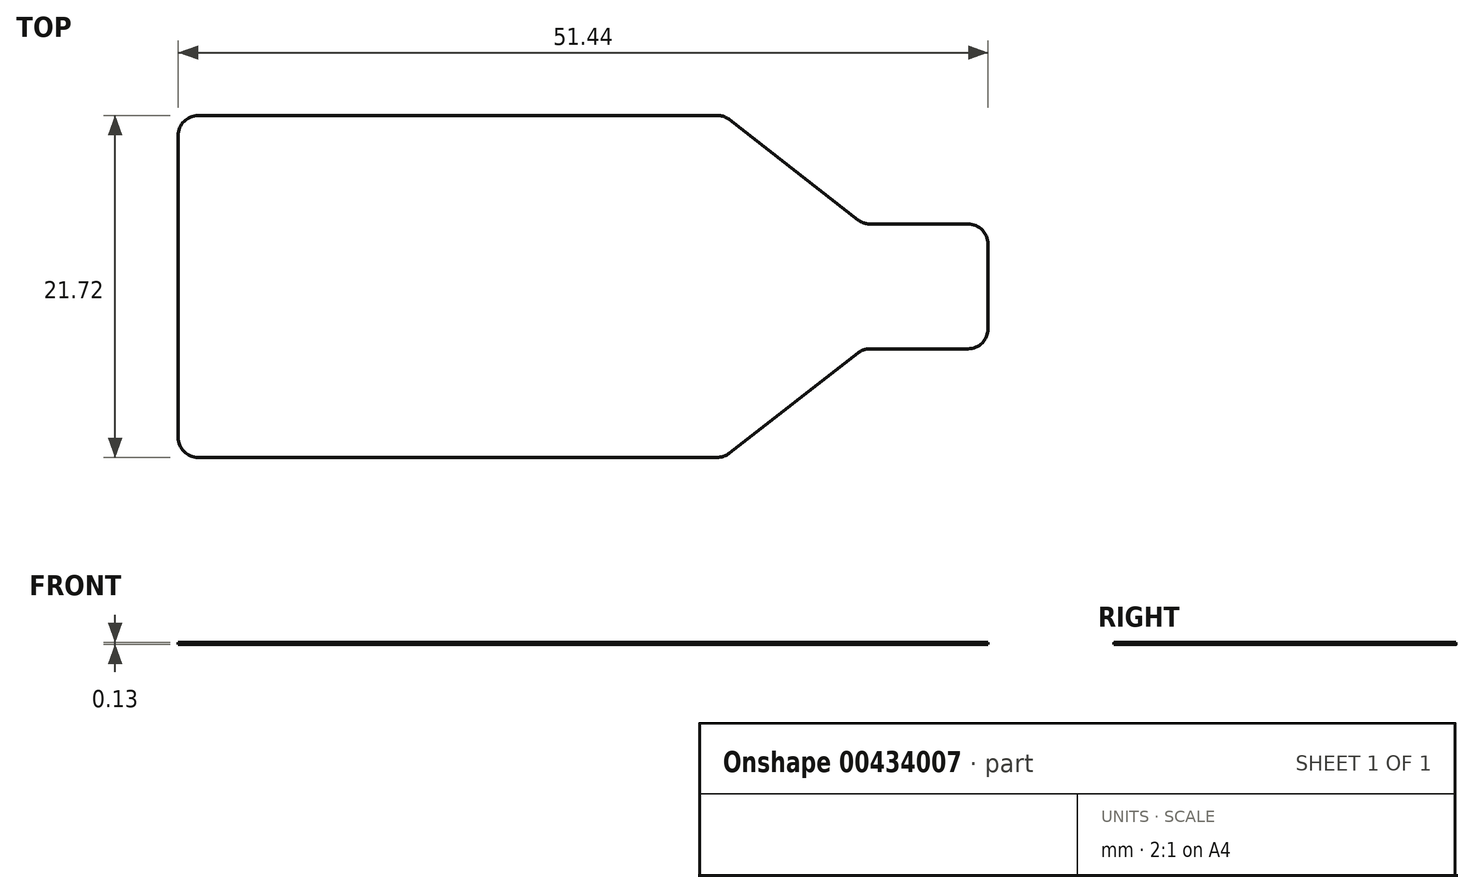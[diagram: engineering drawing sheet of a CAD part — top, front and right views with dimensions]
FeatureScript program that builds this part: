
annotation { "Feature Type Name" : "Feature", "Feature Type Description" : "" }
export const myFeature = defineFeature(function(context is Context, id is Id, definition is map)
    precondition{}
    {
        {
            var Q0;
            Q0=qCreatedBy(makeId("Top.planeOp"),FACE);
            var sketch = newSketch(context, id + "F0", { "sketchPlane" : qUnion([Q0])});
            skLineSegment(sketch, "E0", {"start": v(0, 0) * mm, "end": v(-58.06, 0) * mm, "construction": true});
            skLineSegment(sketch, "E1", {"start": v(0, 0) * mm, "end": v(0, -2.7) * mm});
            skLineSegment(sketch, "E2", {"start": v(-1.27, -3.96) * mm, "end": v(-7.49, -3.96) * mm});
            skLineSegment(sketch, "E3", {"start": v(-8.27, -4.23) * mm, "end": v(-16.42, -10.59) * mm});
            skLineSegment(sketch, "E4", {"start": v(-50.16, -10.86) * mm, "end": v(-17.2, -10.86) * mm});
            skLineSegment(sketch, "E5", {"start": v(-51.44, -9.59) * mm, "end": v(-51.44, 0) * mm});
            skLineSegment(sketch, "E6.MirrorCS", {"start": v(0, 0) * mm, "end": v(0, 2.7) * mm});
            skLineSegment(sketch, "E7.MirrorCS", {"start": v(-1.27, 3.96) * mm, "end": v(-7.49, 3.96) * mm});
            skLineSegment(sketch, "E8.MirrorCS", {"start": v(-8.27, 4.23) * mm, "end": v(-16.42, 10.59) * mm});
            skLineSegment(sketch, "E9.MirrorCS", {"start": v(-17.2, 10.86) * mm, "end": v(-50.17, 10.86) * mm});
            skLineSegment(sketch, "E10.MirrorCS", {"start": v(-51.44, 9.59) * mm, "end": v(-51.44, 0) * mm});
            skPoint(sketch, "E11.visualSharp", {"position": v(-51.44, 10.86) * mm});
            skArc(sketch, "E11.filletArc", {"start": v(-50.17, 10.86) * mm, "mid": v(-51.06, 10.49) * mm, "end": v(-51.44, 9.59) * mm});
            skPoint(sketch, "E12.visualSharp", {"position": v(-51.44, -10.86) * mm});
            skArc(sketch, "E12.filletArc", {"start": v(-51.44, -9.59) * mm, "mid": v(-51.06, -10.49) * mm, "end": v(-50.16, -10.86) * mm});
            skPoint(sketch, "E13.visualSharp", {"position": v(0, 3.96) * mm});
            skArc(sketch, "E13.filletArc", {"start": v(0, 2.7) * mm, "mid": v(-0.37, 3.6) * mm, "end": v(-1.27, 3.96) * mm});
            skPoint(sketch, "E14.visualSharp", {"position": v(0, -3.96) * mm});
            skArc(sketch, "E14.filletArc", {"start": v(-1.27, -3.96) * mm, "mid": v(-0.37, -3.6) * mm, "end": v(0, -2.7) * mm});
            skPoint(sketch, "E15.visualSharp", {"position": v(-7.92, 3.96) * mm});
            skArc(sketch, "E15.filletArc", {"start": v(-8.27, 4.23) * mm, "mid": v(-7.9, 4.03) * mm, "end": v(-7.49, 3.96) * mm});
            skPoint(sketch, "E16.visualSharp", {"position": v(-16.76, 10.86) * mm});
            skArc(sketch, "E16.filletArc", {"start": v(-16.42, 10.59) * mm, "mid": v(-16.79, 10.79) * mm, "end": v(-17.2, 10.86) * mm});
            skPoint(sketch, "E17.visualSharp", {"position": v(-7.92, -3.96) * mm});
            skArc(sketch, "E17.filletArc", {"start": v(-7.49, -3.96) * mm, "mid": v(-7.9, -4.03) * mm, "end": v(-8.27, -4.23) * mm});
            skPoint(sketch, "E18.visualSharp", {"position": v(-16.76, -10.86) * mm});
            skArc(sketch, "E18.filletArc", {"start": v(-17.2, -10.86) * mm, "mid": v(-16.79, -10.79) * mm, "end": v(-16.42, -10.59) * mm});
            skSolve(sketch);
        }
        {
            var Q0;
            Q0 = qSketchRegion(id + "F0", true);
            var Q1;
            Q1 = qConstructionFilter(qBodyType(qCreatedBy(id + "F0" ,EDGE), BodyType.WIRE), ConstructionObject.NO);
            extrude(context, id + "F1", {"entities" : qUnion([Q0]), "surfaceEntities" : qUnion([Q1]), "depth" : 0.13 * mm});
        }
        {
            var Q0;
            Q0=makeQuery(id+"F1.opExtrude","CAP_FACE",FACE,{"disambiguationData":[OSD([sQuery(id+"F0.wireOp",EDGE,"E1"),sQuery(id+"F0.wireOp",EDGE,"E2"),sQuery(id+"F0.wireOp",EDGE,"E3"),sQuery(id+"F0.wireOp",EDGE,"E4"),sQuery(id+"F0.wireOp",EDGE,"E5"),sQuery(id+"F0.wireOp",EDGE,"E6.MirrorCS"),sQuery(id+"F0.wireOp",EDGE,"E7.MirrorCS"),sQuery(id+"F0.wireOp",EDGE,"E8.MirrorCS"),sQuery(id+"F0.wireOp",EDGE,"E9.MirrorCS"),sQuery(id+"F0.wireOp",EDGE,"E10.MirrorCS"),sQuery(id+"F0.wireOp",EDGE,"E11.filletArc"),sQuery(id+"F0.wireOp",EDGE,"E12.filletArc"),sQuery(id+"F0.wireOp",EDGE,"E13.filletArc"),sQuery(id+"F0.wireOp",EDGE,"E14.filletArc"),sQuery(id+"F0.wireOp",EDGE,"E15.filletArc"),sQuery(id+"F0.wireOp",EDGE,"E16.filletArc"),sQuery(id+"F0.wireOp",EDGE,"E17.filletArc"),sQuery(id+"F0.wireOp",EDGE,"E18.filletArc")])],"isStart":false});
            var sketch = newSketch(context, id + "F2", { "sketchPlane" : qUnion([Q0])});
            skArc(sketch, "E19", {"start": v(-40.48, 10.86) * mm, "mid": v(-43.51, 0) * mm, "end": v(-40.48, -10.86) * mm});
            skLineSegment(sketch, "E20", {"start": v(-40.48, 10.86) * mm, "end": v(-50.17, 10.86) * mm});
            skLineSegment(sketch, "E21", {"start": v(-40.48, -10.86) * mm, "end": v(-50.17, -10.86) * mm});
            skLineSegment(sketch, "E22", {"start": v(-51.44, 9.59) * mm, "end": v(-51.44, -9.59) * mm});
            skArc(sketch, "E23", {"start": v(-50.17, 10.86) * mm, "mid": v(-51.06, 10.49) * mm, "end": v(-51.44, 9.59) * mm});
            skArc(sketch, "E24", {"start": v(-51.44, -9.59) * mm, "mid": v(-51.06, -10.49) * mm, "end": v(-50.17, -10.86) * mm});
            skLineSegment(sketch, "E25.0", {"start": v(-17.2, 10.86) * mm, "end": v(-50.17, 10.86) * mm, "construction": true});
            skLineSegment(sketch, "E26.0", {"start": v(-8.27, 4.23) * mm, "end": v(-16.42, 10.59) * mm, "construction": true});
            skLineSegment(sketch, "E27.0", {"start": v(-1.27, 3.96) * mm, "end": v(-7.49, 3.96) * mm, "construction": true});
            skSolve(sketch);
        }
        {
            var Q0;
            Q0 = qConstructionFilter(qBodyType(qCreatedBy(id + "F2" ,EDGE), BodyType.WIRE), ConstructionObject.NO);
            extrude(context, id + "F3", {"bodyType" : ToolBodyType.SURFACE, "surfaceEntities" : qUnion([Q0]), "depth" : 0.13 * mm, "offsetDistance" : 25.4 * mm});
        }
    });
